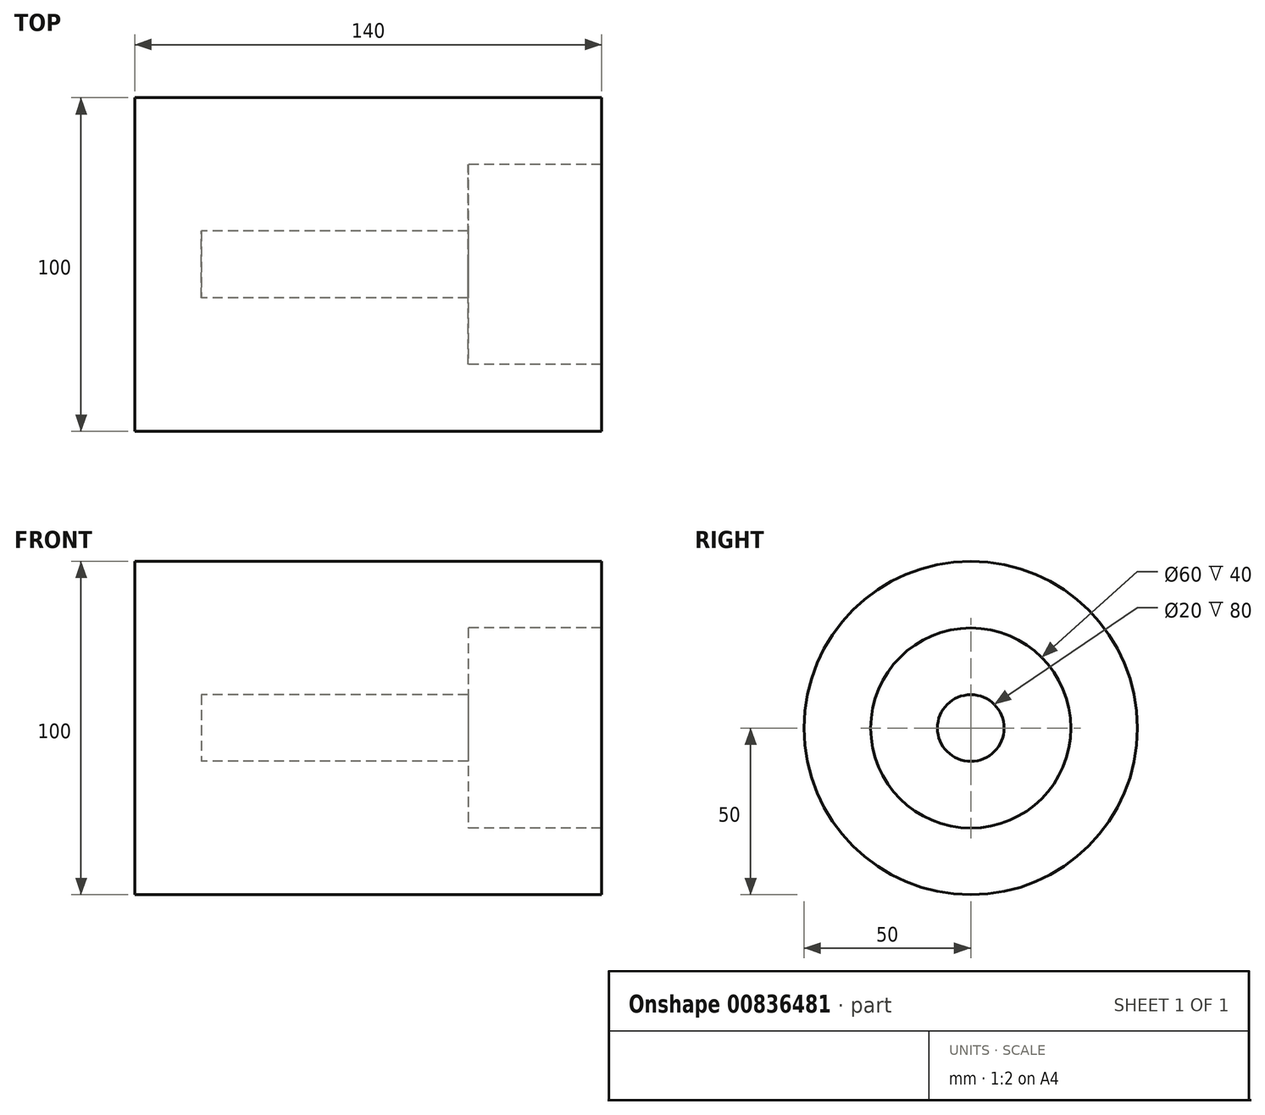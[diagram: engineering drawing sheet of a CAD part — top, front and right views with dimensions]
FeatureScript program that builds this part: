
annotation { "Feature Type Name" : "Feature", "Feature Type Description" : "" }
export const myFeature = defineFeature(function(context is Context, id is Id, definition is map)
    precondition{}
    {
        {
            var Q0;
            Q0=qCreatedBy(makeId("Top.planeOp"),FACE);
            var sketch = newSketch(context, id + "F0", { "sketchPlane" : qUnion([Q0])});
            skLineSegment(sketch, "E0.bottom", {"start": v(70, 50) * mm, "end": v(-70, 50) * mm});
            skLineSegment(sketch, "E0.top", {"start": v(70, -50) * mm, "end": v(-70, -50) * mm, "construction": true});
            skLineSegment(sketch, "E0.left", {"start": v(70, 50) * mm, "end": v(70, 30) * mm});
            skLineSegment(sketch, "E0.right", {"start": v(-70, 50) * mm, "end": v(-70, 0) * mm});
            skPoint(sketch, "E0.middle", {"position": v(0, 0) * mm});
            skLineSegment(sketch, "E1", {"start": v(30, 10) * mm, "end": v(30, 30) * mm});
            skLineSegment(sketch, "E2", {"start": v(30, 30) * mm, "end": v(70, 30) * mm});
            skLineSegment(sketch, "E3", {"start": v(-50, 0) * mm, "end": v(-50, 10) * mm});
            skLineSegment(sketch, "E4", {"start": v(-50, 10) * mm, "end": v(30, 10) * mm});
            skLineSegment(sketch, "E5", {"start": v(30, -10) * mm, "end": v(30, -30) * mm, "construction": true});
            skLineSegment(sketch, "E6", {"start": v(30, -30) * mm, "end": v(70, -30) * mm, "construction": true});
            skLineSegment(sketch, "E7", {"start": v(-50, -10) * mm, "end": v(30, -10) * mm, "construction": true});
            skPoint(sketch, "E8.orphan", {"position": v(30, 0) * mm});
            skLineSegment(sketch, "E9.trimOffspring", {"start": v(70, -30) * mm, "end": v(70, -50) * mm, "construction": true});
            skLineSegment(sketch, "E10", {"start": v(-50, 0) * mm, "end": v(73.53, 0) * mm, "construction": true});
            skPoint(sketch, "E11.orphan", {"position": v(-70, 0) * mm});
            skLineSegment(sketch, "E12", {"start": v(-70, 0) * mm, "end": v(-50, 0) * mm});
            skLineSegment(sketch, "E13", {"start": v(-70, 0) * mm, "end": v(-70, -50) * mm, "construction": true});
            skLineSegment(sketch, "E14", {"start": v(-50, -10) * mm, "end": v(-50, 0) * mm, "construction": true});
            skSolve(sketch);
        }
        {
            var Q0;
            {var subQ3=sQuery(id+"F0.wireOp",EDGE,"E0.bottom");Q0=makeQuery(id+"F0.imprint","IMPRINT",FACE,{"disambiguationData":[TD([[makeQuery(id+"F0.imprint","IMPRINT",EDGE,{"derivedFrom":subQ3}),1.0]])]});}
            var Q1;
            Q1=sQuery(id+"F0.wireOp",EDGE,"E10");
            revolve(context, id + "F1", {"surfaceOperationType" : NewSurfaceOperationType.NEW, "entities" : qUnion([Q0]), "axis" : qUnion([Q1]), "revolveType" : RevolveType.ONE_DIRECTION, "angle" : 360 * degree});
        }
    });
